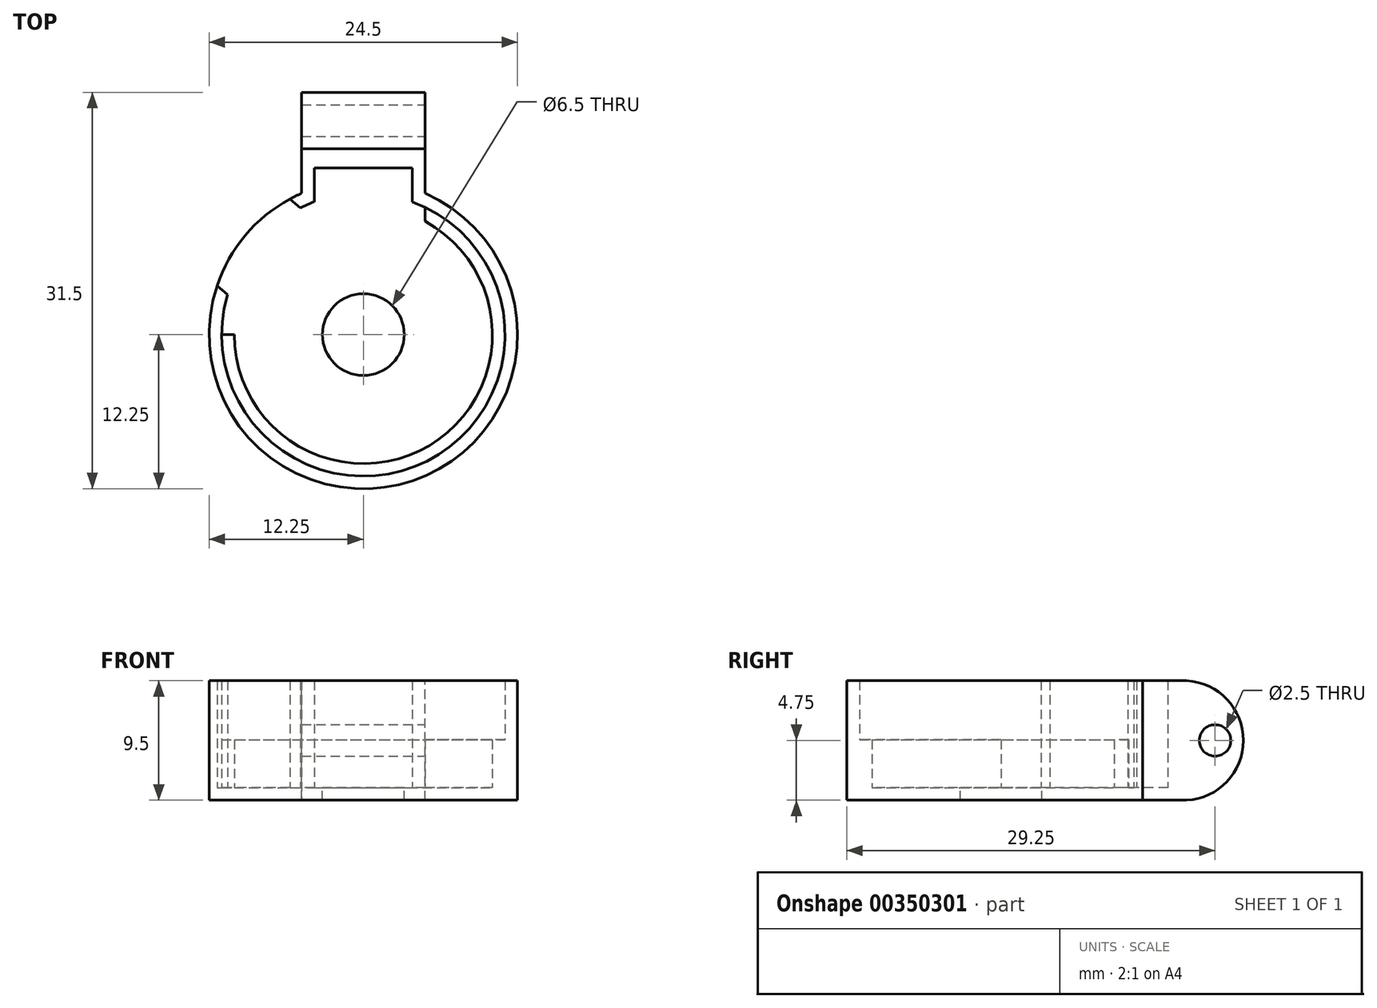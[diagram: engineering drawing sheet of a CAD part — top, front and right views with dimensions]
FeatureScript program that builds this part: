
annotation { "Feature Type Name" : "Feature", "Feature Type Description" : "" }
export const myFeature = defineFeature(function(context is Context, id is Id, definition is map)
    precondition{}
    {
        {
            var Q0;
            Q0=qCreatedBy(makeId("Top.planeOp"),FACE);
            var sketch = newSketch(context, id + "F0", { "sketchPlane" : qUnion([Q0])});
            skCircle(sketch, "E0", {"center": v(0, 0) * mm, "radius": 11.25 * mm});
            skCircle(sketch, "E1", {"center": v(0, 0) * mm, "radius": 3.25 * mm});
            skCircle(sketch, "E2", {"center": v(0, 0) * mm, "radius": 12.25 * mm});
            skLineSegment(sketch, "E3.bottom", {"start": v(-3.9, 13.25) * mm, "end": v(3.9, 13.25) * mm});
            skLineSegment(sketch, "E3.left", {"start": v(-3.9, 13.25) * mm, "end": v(-3.9, 11.61) * mm});
            skLineSegment(sketch, "E3.right", {"start": v(3.9, 13.25) * mm, "end": v(3.9, 11.61) * mm});
            skPoint(sketch, "E3.middle", {"position": v(0, 12.25) * mm});
            skLineSegment(sketch, "E4.bottom", {"start": v(-4.9, 19.25) * mm, "end": v(4.9, 19.25) * mm});
            skLineSegment(sketch, "E4.left", {"start": v(-4.9, 19.25) * mm, "end": v(-4.9, 11.23) * mm});
            skLineSegment(sketch, "E4.right", {"start": v(4.9, 19.25) * mm, "end": v(4.9, 11.23) * mm});
            skLineSegment(sketch, "E5", {"start": v(0, 19.25) * mm, "end": v(0, 13.25) * mm, "construction": true});
            skLineSegment(sketch, "E6", {"start": v(-3.9, 11.61) * mm, "end": v(-3.9, 10.55) * mm});
            skLineSegment(sketch, "E7", {"start": v(3.9, 11.61) * mm, "end": v(3.9, 10.55) * mm});
            skLineSegment(sketch, "E8", {"start": v(0, 0) * mm, "end": v(-9.38, 7.87) * mm, "construction": true});
            skLineSegment(sketch, "E9", {"start": v(-5.84, 10.77) * mm, "end": v(-5, 10.07) * mm});
            skLineSegment(sketch, "E10", {"start": v(-11.62, 3.88) * mm, "end": v(-10.8, 3.18) * mm});
            skCircle(sketch, "E11", {"center": v(0, 0) * mm, "radius": 10.25 * mm});
            skLineSegment(sketch, "E12", {"start": v(4.9, 10.13) * mm, "end": v(4.9, 9) * mm});
            skLineSegment(sketch, "E13", {"start": v(-11.25, 0) * mm, "end": v(-10.25, 0) * mm});
            skSolve(sketch);
        }
        {
            var Q0;
            {var subQ0=sQuery(id+"F0.wireOp",EDGE,"E6");Q0=makeQuery(id+"F0.imprint","IMPRINT",FACE,{"disambiguationData":[TD([[makeQuery(id+"F0.imprint","IMPRINT",EDGE,{"derivedFrom":subQ0}),1.0]])]});}
            var Q1;
            Q1=makeQuery(id+"F0.imprint","IMPRINT",FACE,{"disambiguationData":[TD([[makeQuery(id+"F0.imprint","IMPRINT",EDGE,{"derivedFrom":sQuery(id+"F0.wireOp",EDGE,"E3.bottom")}),-1.0]])]});
            var Q2;
            {var subQ0=sQuery(id+"F0.wireOp",EDGE,"E6");Q2=makeQuery(id+"F0.imprint","IMPRINT",FACE,{"disambiguationData":[TD([[makeQuery(id+"F0.imprint","IMPRINT",EDGE,{"derivedFrom":subQ0}),-1.0]])]});}
            var Q3;
            Q3=makeQuery(id+"F0.imprint","IMPRINT",FACE,{"disambiguationData":[TD([[makeQuery(id+"F0.imprint","IMPRINT",EDGE,{"derivedFrom":sQuery(id+"F0.wireOp",EDGE,"E3.bottom")}),1.0]])]});
            var Q4;
            {var subQ3=sQuery(id+"F0.wireOp",EDGE,"E7");Q4=makeQuery(id+"F0.imprint","IMPRINT",FACE,{"disambiguationData":[TD([[makeQuery(id+"F0.imprint","IMPRINT",EDGE,{"derivedFrom":subQ3}),1.0]])]});}
            var Q5;
            {var subQ0=sQuery(id+"F0.wireOp",EDGE,"E9");Q5=makeQuery(id+"F0.imprint","IMPRINT",FACE,{"disambiguationData":[TD([[makeQuery(id+"F0.imprint","IMPRINT",EDGE,{"derivedFrom":subQ0}),-1.0]])]});}
            var Q6;
            Q6=makeQuery(id+"F0.imprint","IMPRINT",FACE,{"disambiguationData":[TD([[makeQuery(id+"F0.imprint","IMPRINT",EDGE,{"derivedFrom":sQuery(id+"F0.wireOp",EDGE,"E1")}),-1.0]])]});
            var Q7;
            {var subQ3=sQuery(id+"F0.wireOp",EDGE,"E12");Q7=makeQuery(id+"F0.imprint","IMPRINT",FACE,{"disambiguationData":[TD([[makeQuery(id+"F0.imprint","IMPRINT",EDGE,{"derivedFrom":subQ3}),-1.0]])]});}
            var Q8;
            {var subQ0=sQuery(id+"F0.wireOp",EDGE,"E12");Q8=makeQuery(id+"F0.imprint","IMPRINT",FACE,{"disambiguationData":[TD([[makeQuery(id+"F0.imprint","IMPRINT",EDGE,{"derivedFrom":subQ0}),1.0]])]});}
            extrude(context, id + "F1", {"entities" : qUnion([Q0, Q1, Q2, Q3, Q4, Q5, Q6, Q7, Q8]), "oppositeDirection" : true, "depth" : 1 * mm});
        }
        {
            var Q0;
            {var subQ0=sQuery(id+"F0.wireOp",EDGE,"E6");Q0=makeQuery(id+"F0.imprint","IMPRINT",FACE,{"disambiguationData":[TD([[makeQuery(id+"F0.imprint","IMPRINT",EDGE,{"derivedFrom":subQ0}),-1.0]])]});}
            var Q1;
            Q1=makeQuery(id+"F0.imprint","IMPRINT",FACE,{"disambiguationData":[TD([[makeQuery(id+"F0.imprint","IMPRINT",EDGE,{"derivedFrom":sQuery(id+"F0.wireOp",EDGE,"E3.bottom")}),1.0]])]});
            var Q2;
            {var subQ3=sQuery(id+"F0.wireOp",EDGE,"E7");Q2=makeQuery(id+"F0.imprint","IMPRINT",FACE,{"disambiguationData":[TD([[makeQuery(id+"F0.imprint","IMPRINT",EDGE,{"derivedFrom":subQ3}),1.0]])]});}
            extrude(context, id + "F2", {"entities" : qUnion([Q0, Q1, Q2]), "operationType" : NewBodyOperationType.ADD, "depth" : 8.5 * mm});
        }
        {
            var Q0;
            {var subQ0=sQuery(id+"F0.wireOp",EDGE,"E12");Q0=makeQuery(id+"F0.imprint","IMPRINT",FACE,{"disambiguationData":[TD([[makeQuery(id+"F0.imprint","IMPRINT",EDGE,{"derivedFrom":subQ0}),1.0]])]});}
            extrude(context, id + "F3", {"entities" : qUnion([Q0]), "operationType" : NewBodyOperationType.ADD, "depth" : 3.8 * mm});
        }
        {
            var Q0;
            {var subQ0=sQuery(id+"F0.wireOp",EDGE,"E4.right");Q0=makeQuery(id+"F2.boolean.opBoolean","MERGE",FACE,{"derivedFrom":[makeQuery(id+"F1.opExtrude","SWEPT_FACE",FACE,{"disambiguationData":[OSD([subQ0])]}),makeQuery(id+"F2.opExtrude","SWEPT_FACE",FACE,{"disambiguationData":[OSD([subQ0])]})]});}
            var sketch = newSketch(context, id + "F4", { "sketchPlane" : qUnion([Q0])});
            skArc(sketch, "E14", {"start": v(14.75, -1) * mm, "mid": v(19.25, 3.75) * mm, "end": v(14.75, 8.5) * mm});
            skLineSegment(sketch, "E15", {"start": v(14.75, 8.5) * mm, "end": v(14.75, -1) * mm, "construction": true});
            skCircle(sketch, "E16", {"center": v(17, 3.75) * mm, "radius": 1.25 * mm});
            skLineSegment(sketch, "E17", {"start": v(14.75, 3.75) * mm, "end": v(19.25, 3.75) * mm, "construction": true});
            skSolve(sketch);
        }
        {
            var Q0;
            {var subQ0=sQuery(id+"F4.wireOp",EDGE,"E14");var subQ1=sQuery(id+"F0.wireOp",EDGE,"E4.right");var subQ2=makeQuery(id+"F2.opExtrude","CAP_EDGE",EDGE,{"disambiguationData":[OSD([subQ1])],"isStart":false});var subQ3=makeQuery(id+"F4.imprint","INTERSECT",VERTEX,{"derivedFrom":[subQ2,subQ0]});Q0=makeQuery(id+"F4.imprint","IMPRINT",FACE,{"disambiguationData":[TD([[makeQuery(id+"F4.imprint","IMPRINT",EDGE,{"disambiguationData":[TD([[subQ3,1.0]])],"derivedFrom":subQ0}),-1.0]])]});}
            var Q1;
            {var subQ0=sQuery(id+"F4.wireOp",EDGE,"E14");var subQ1=sQuery(id+"F0.wireOp",EDGE,"E4.right");var subQ2=makeQuery(id+"F1.opExtrude","CAP_EDGE",EDGE,{"disambiguationData":[OSD([subQ1])],"isStart":false});var subQ3=makeQuery(id+"F4.imprint","INTERSECT",VERTEX,{"derivedFrom":[subQ2,subQ0]});Q1=makeQuery(id+"F4.imprint","IMPRINT",FACE,{"disambiguationData":[TD([[makeQuery(id+"F4.imprint","IMPRINT",EDGE,{"disambiguationData":[TD([[subQ3,-1.0]])],"derivedFrom":subQ0}),-1.0]])]});}
            var Q2;
            Q2=makeQuery(id+"F4.imprint","IMPRINT",FACE,{"disambiguationData":[TD([[makeQuery(id+"F4.imprint","IMPRINT",EDGE,{"derivedFrom":sQuery(id+"F4.wireOp",EDGE,"E16")}),1.0]])]});
            extrude(context, id + "F5", {"entities" : qUnion([Q0, Q1, Q2]), "operationType" : NewBodyOperationType.REMOVE, "endBound" : BoundingType.UP_TO_NEXT, "oppositeDirection" : true, "depth" : 25 * mm});
        }
    });
